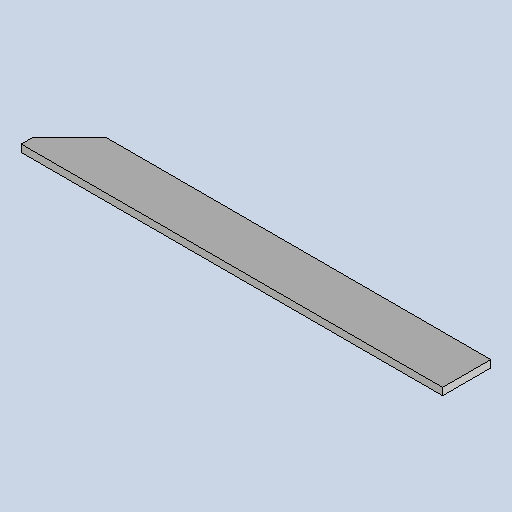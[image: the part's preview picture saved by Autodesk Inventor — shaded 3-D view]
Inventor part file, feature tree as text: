
AUTODESK INVENTOR PART (.ipt)
format: ipt  version: 2025 (Build 290162010, 162A)  size: 109,568 bytes
history: native  units: mm
features: other x2, sheet_metal_op x1, chamfer x1, sketch x1
ambient origin geometry x8: Origin, YZ Plane, XZ Plane, XY Plane, X Axis, Y Axis, Z Axis, Center Point
bodies: Solid1 (feature_tree)
feature tree (5):
  sheet_metal_op  "Face1"
  chamfer  "Chamfer1"  Distance=175.0mm
  sketch  "Sketch1"  dims[d2=20.0mm d3=175.0mm d4=3.0mm d5=15.0mm d6=2.0mm d7=45.0deg]
  other  "Plate1"
  other  "Definition1"
